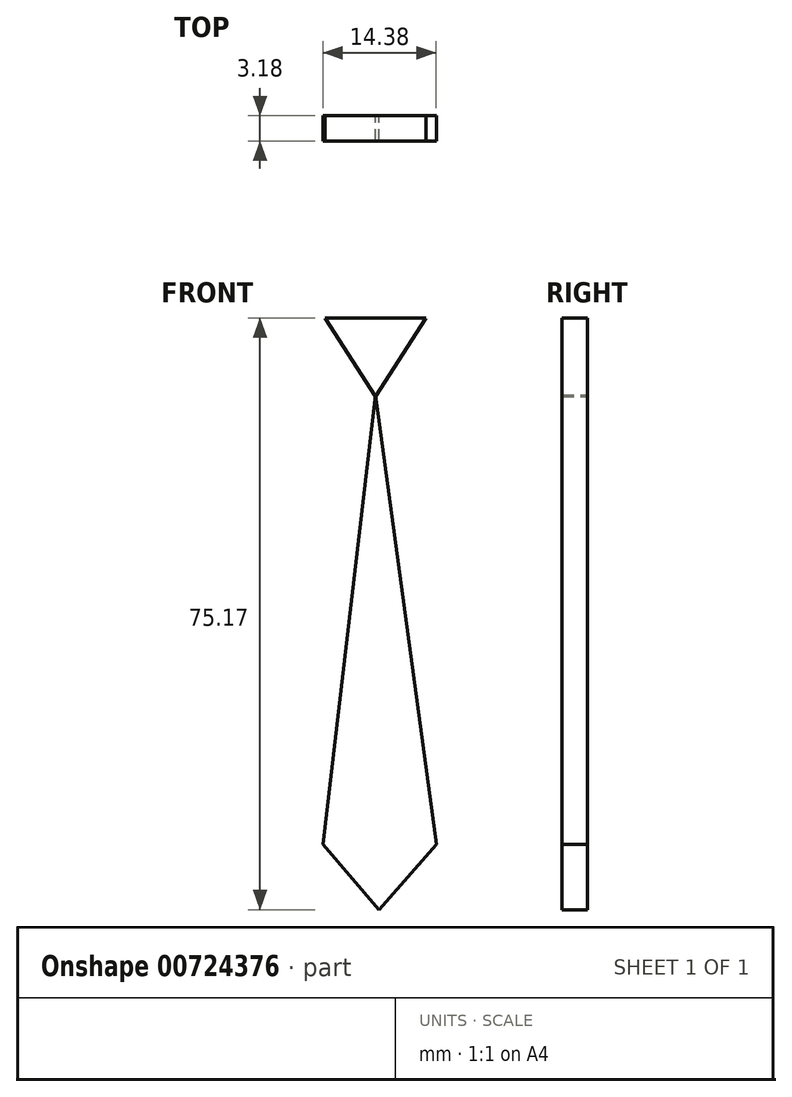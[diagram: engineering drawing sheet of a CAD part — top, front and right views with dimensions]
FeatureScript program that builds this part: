
annotation { "Feature Type Name" : "Feature", "Feature Type Description" : "" }
export const myFeature = defineFeature(function(context is Context, id is Id, definition is map)
    precondition{}
    {
        {
            var Q0;
            Q0=qCreatedBy(makeId("Front.planeOp"),FACE);
            var sketch = newSketch(context, id + "F0", { "sketchPlane" : qUnion([Q0])});
            skLineSegment(sketch, "E0", {"start": v(-54.72, 56.52) * mm, "end": v(-41.87, 56.52) * mm});
            skLineSegment(sketch, "E1", {"start": v(-41.87, 56.52) * mm, "end": v(-48.3, 46.56) * mm});
            skPoint(sketch, "E1.endSnap0", {"position": v(-48.3, 56.52) * mm});
            skLineSegment(sketch, "E2", {"start": v(-48.3, 46.56) * mm, "end": v(-54.72, 56.52) * mm});
            skSolve(sketch);
        }
        {
            var Q0;
            Q0=qCreatedBy(makeId("Front.planeOp"),FACE);
            var sketch = newSketch(context, id + "F1", { "sketchPlane" : qUnion([Q0])});
            skLineSegment(sketch, "E3", {"start": v(-48.3, 46.74) * mm, "end": v(-54.96, -10.37) * mm});
            skLineSegment(sketch, "E4", {"start": v(-54.96, -10.37) * mm, "end": v(-47.84, -18.65) * mm});
            skLineSegment(sketch, "E5", {"start": v(-47.84, -18.65) * mm, "end": v(-54.96, -10.37) * mm});
            skLineSegment(sketch, "E6", {"start": v(-48.3, 46.74) * mm, "end": v(-40.58, -10.37) * mm});
            skLineSegment(sketch, "E7", {"start": v(-40.58, -10.37) * mm, "end": v(-47.84, -18.65) * mm});
            skSolve(sketch);
        }
        {
            var Q0;
            Q0=makeQuery(id+"F1.imprint","IMPRINT",FACE,{"disambiguationData":[TD([[makeQuery(id+"F1.imprint","IMPRINT",EDGE,{"derivedFrom":sQuery(id+"F1.wireOp",EDGE,"E3")}),1.0]])]});
            var Q1;
            Q1=makeQuery(id+"F0.imprint","IMPRINT",FACE,{"disambiguationData":[TD([[makeQuery(id+"F0.imprint","IMPRINT",EDGE,{"derivedFrom":sQuery(id+"F0.wireOp",EDGE,"E0")}),-1.0]])]});
            extrude(context, id + "F2", {"entities" : qUnion([Q0, Q1]), "depth" : 3.18 * mm, "offsetDistance" : 25.4 * mm});
        }
    });
